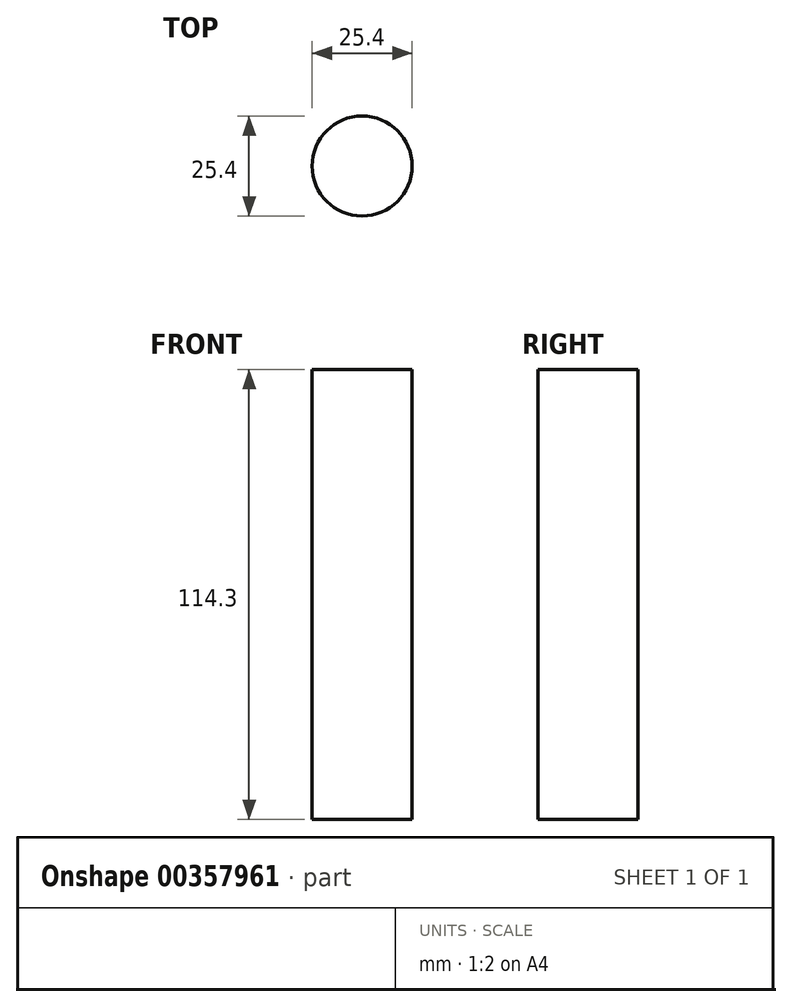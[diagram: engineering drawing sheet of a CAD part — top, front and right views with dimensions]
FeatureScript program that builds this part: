
annotation { "Feature Type Name" : "Feature", "Feature Type Description" : "" }
export const myFeature = defineFeature(function(context is Context, id is Id, definition is map)
    precondition{}
    {
        {
            var Q0;
            Q0=qCreatedBy(makeId("Top.planeOp"),FACE);
            var sketch = newSketch(context, id + "F0", { "sketchPlane" : qUnion([Q0])});
            skCircle(sketch, "E0", {"center": v(0, 0) * mm, "radius": 12.7 * mm});
            skSolve(sketch);
        }
        {
            var Q0;
            Q0 = qSketchRegion(id + "F0", true);
            extrude(context, id + "F1", {"entities" : qUnion([Q0]), "depth" : 114.3 * mm});
        }
    });
